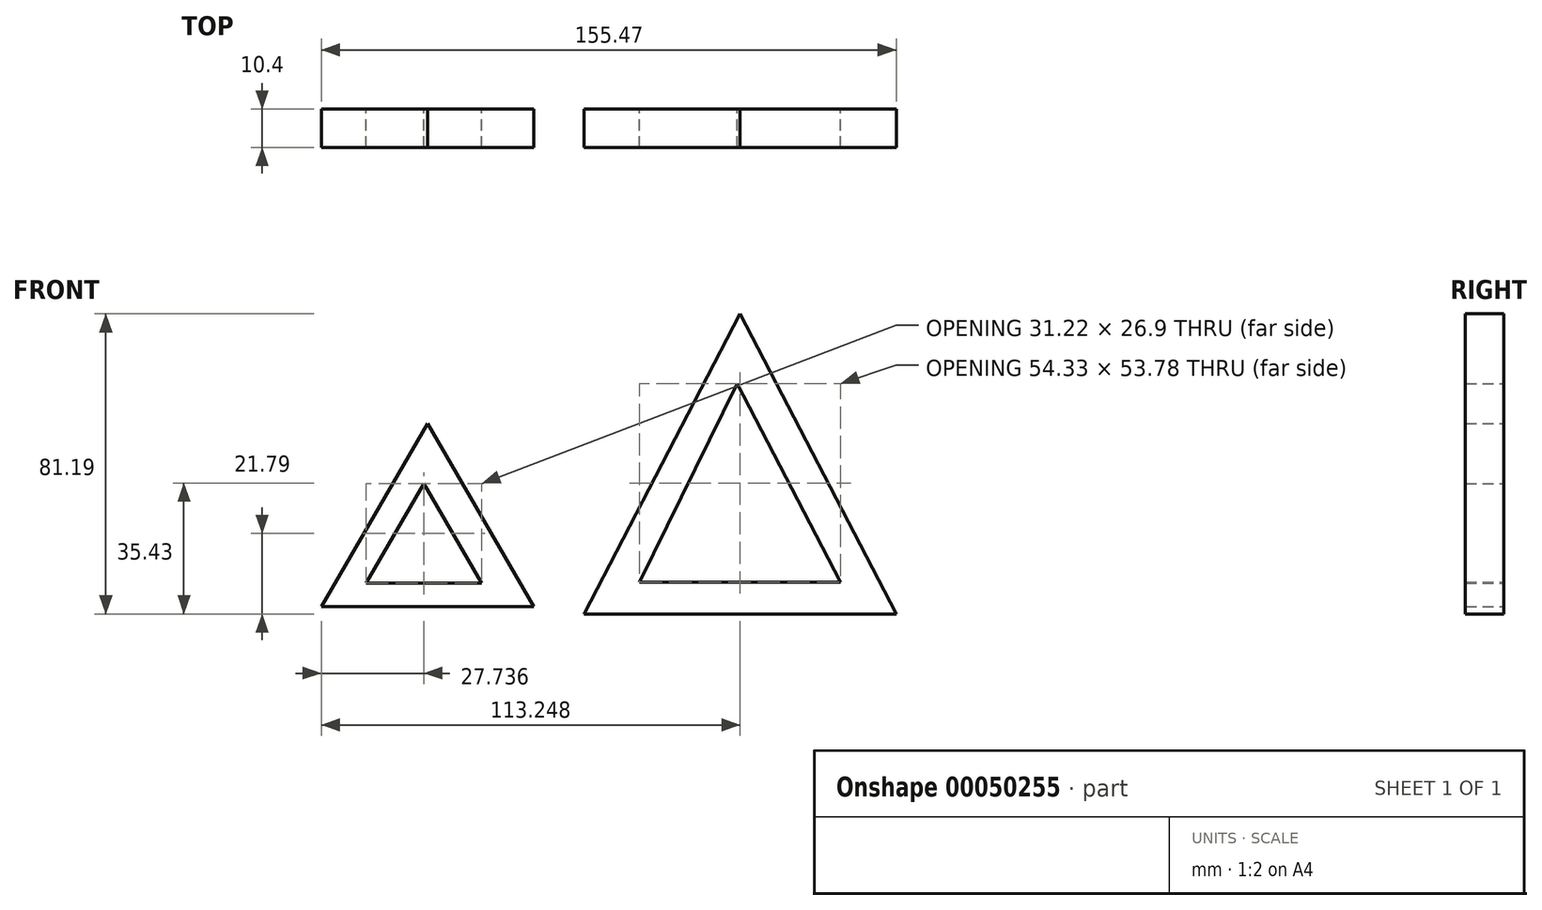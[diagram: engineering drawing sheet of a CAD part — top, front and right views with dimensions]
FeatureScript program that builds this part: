
annotation { "Feature Type Name" : "Feature", "Feature Type Description" : "" }
export const myFeature = defineFeature(function(context is Context, id is Id, definition is map)
    precondition{}
    {
        {
            var Q0;
            Q0=qCreatedBy(makeId("Front.planeOp"),FACE);
            var sketch = newSketch(context, id + "F0", { "sketchPlane" : qUnion([Q0])});
            skLineSegment(sketch, "E0", {"start": v(-64.5, 16.9) * mm, "end": v(-7.12, 16.9) * mm});
            skLineSegment(sketch, "E1", {"start": v(-7.12, 16.9) * mm, "end": v(-35.82, 16.9) * mm, "construction": true});
            skLineSegment(sketch, "E2", {"start": v(-7.12, 16.9) * mm, "end": v(-35.82, 66.34) * mm});
            skLineSegment(sketch, "E3", {"start": v(-35.82, 66.34) * mm, "end": v(-64.5, 16.9) * mm});
            skLineSegment(sketch, "E4", {"start": v(-53.11, 23.2) * mm, "end": v(-21.16, 23.2) * mm});
            skLineSegment(sketch, "E5", {"start": v(-21.16, 23.2) * mm, "end": v(-36.77, 50.1) * mm});
            skLineSegment(sketch, "E6", {"start": v(-36.77, 50.1) * mm, "end": v(-52.38, 23.2) * mm});
            skLineSegment(sketch, "E7", {"start": v(6.51, 14.86) * mm, "end": v(90.96, 14.86) * mm});
            skLineSegment(sketch, "E8", {"start": v(90.96, 14.86) * mm, "end": v(48.74, 14.86) * mm, "construction": true});
            skLineSegment(sketch, "E9", {"start": v(90.96, 14.86) * mm, "end": v(48.74, 96.05) * mm});
            skLineSegment(sketch, "E10", {"start": v(48.74, 96.05) * mm, "end": v(6.51, 14.86) * mm});
            skLineSegment(sketch, "E11", {"start": v(21.57, 23.4) * mm, "end": v(75.9, 23.4) * mm});
            skLineSegment(sketch, "E12", {"start": v(75.9, 23.4) * mm, "end": v(47.94, 77.18) * mm});
            skLineSegment(sketch, "E13", {"start": v(47.94, 77.18) * mm, "end": v(21.57, 23.4) * mm});
            skSolve(sketch);
        }
        {
            var Q0;
            Q0=makeQuery(id+"F0.imprint","IMPRINT",FACE,{"disambiguationData":[TD([[makeQuery(id+"F0.imprint","IMPRINT",EDGE,{"derivedFrom":sQuery(id+"F0.wireOp",EDGE,"E7")}),1.0]])]});
            var Q1;
            Q1=makeQuery(id+"F0.imprint","IMPRINT",FACE,{"disambiguationData":[TD([[makeQuery(id+"F0.imprint","IMPRINT",EDGE,{"derivedFrom":sQuery(id+"F0.wireOp",EDGE,"E0")}),1.0]])]});
            extrude(context, id + "F1", {"entities" : qUnion([Q0, Q1]), "depth" : 10.4 * mm});
        }
    });
